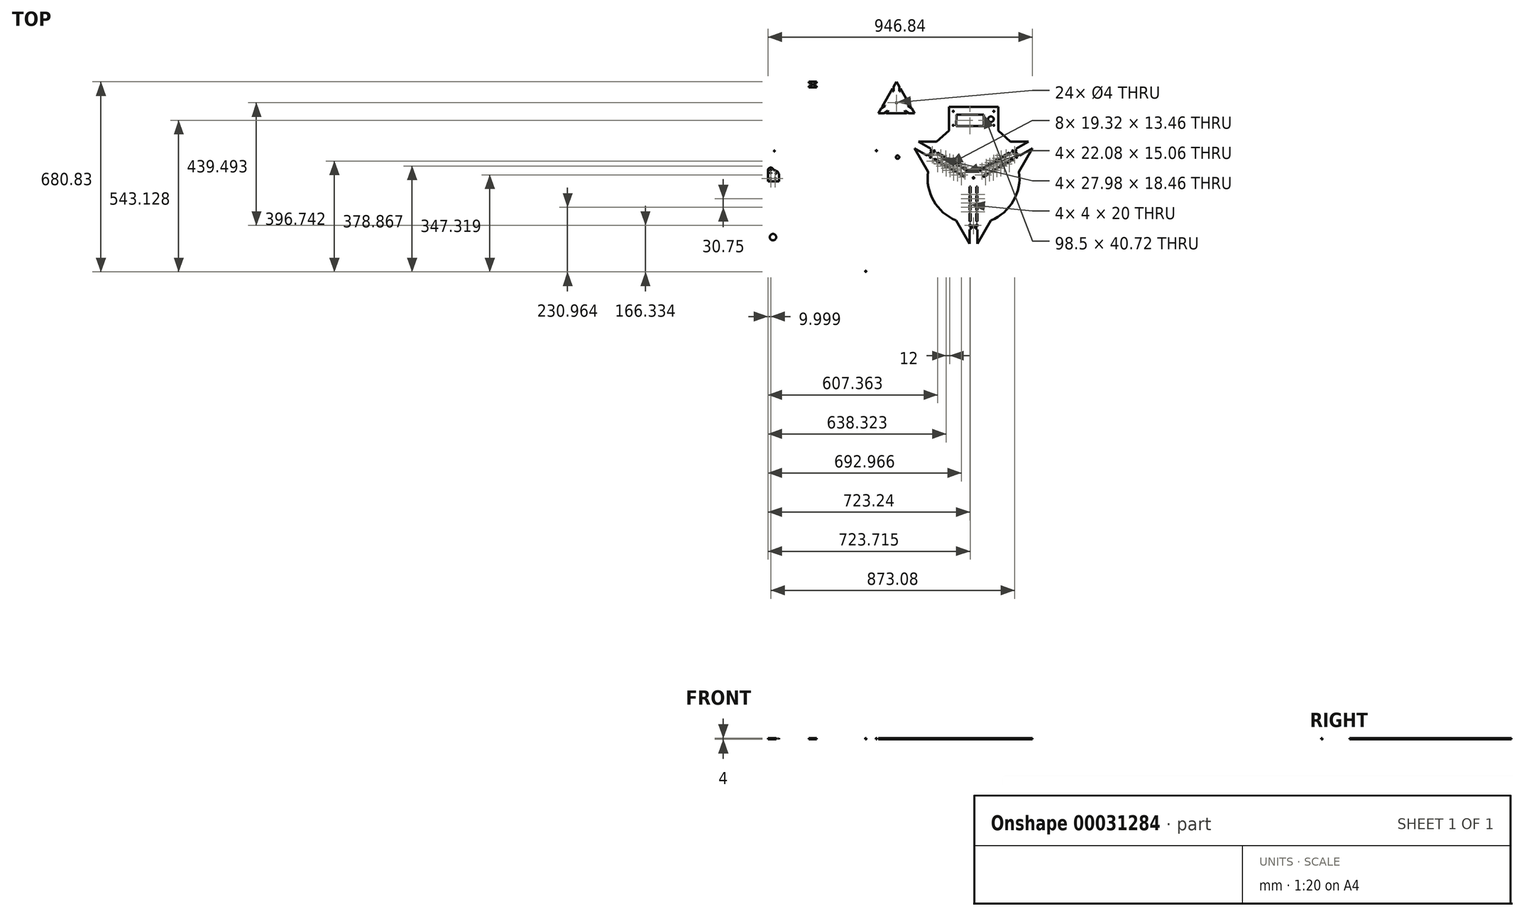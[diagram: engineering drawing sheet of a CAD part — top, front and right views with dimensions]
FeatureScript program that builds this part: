
annotation { "Feature Type Name" : "Feature", "Feature Type Description" : "" }
export const myFeature = defineFeature(function(context is Context, id is Id, definition is map)
    precondition{}
    {
        {
            var Q0;
            Q0=qCreatedBy(makeId("Top.planeOp"),FACE);
            var sketch = newSketch(context, id + "F0", { "sketchPlane" : qUnion([Q0])});
            skCircle(sketch, "E0", {"center": v(-448.83, 54.99) * mm, "radius": 1.5 * mm});
            skCircle(sketch, "E1", {"center": v(-448.8, 86.08) * mm, "radius": 1.5 * mm});
            skCircle(sketch, "E2", {"center": v(-453.84, -253.52) * mm, "radius": 11.5 * mm});
            skCircle(sketch, "E3", {"center": v(-386.12, -280.64) * mm, "radius": 2 * mm});
            skCircle(sketch, "E4", {"center": v(-423.42, -280.64) * mm, "radius": 2 * mm});
            skCircle(sketch, "E5", {"center": v(-469.5, -280.64) * mm, "radius": 2 * mm});
            skCircle(sketch, "E6", {"center": v(-438.44, -237.96) * mm, "radius": 1.5 * mm});
            skCircle(sketch, "E7", {"center": v(-469.53, -237.9) * mm, "radius": 1.5 * mm});
            skCircle(sketch, "E8", {"center": v(-439.73, -262.53) * mm, "radius": 1.5 * mm});
            skCircle(sketch, "E9", {"center": v(-448.28, -269) * mm, "radius": 1.5 * mm});
            skCircle(sketch, "E10", {"center": v(-438.44, -291.39) * mm, "radius": 1.5 * mm});
            skCircle(sketch, "E11", {"center": v(-469.55, -291.39) * mm, "radius": 1.5 * mm});
            skCircle(sketch, "E12", {"center": v(-469.55, -269) * mm, "radius": 1.5 * mm});
            skCircle(sketch, "E13", {"center": v(-83.7, 56.02) * mm, "radius": 2 * mm});
            skCircle(sketch, "E14", {"center": v(-231.13, -199.23) * mm, "radius": 2 * mm});
            skCircle(sketch, "E15", {"center": v(-378.53, 55.85) * mm, "radius": 2 * mm});
            skCircle(sketch, "E16", {"center": v(-231.13, -29.98) * mm, "radius": 177.5 * mm});
            skLineSegment(sketch, "E17", {"start": v(-11.84, 302.96) * mm, "end": v(-1.84, 285.64) * mm});
            skLineSegment(sketch, "E18", {"start": v(-1.84, 285.64) * mm, "end": v(-1.84, 258.8) * mm});
            skLineSegment(sketch, "E19", {"start": v(-1.84, 258.8) * mm, "end": v(2.16, 258.8) * mm});
            skLineSegment(sketch, "E20", {"start": v(2.16, 258.8) * mm, "end": v(2.16, 278.7) * mm});
            skLineSegment(sketch, "E21", {"start": v(2.16, 278.7) * mm, "end": v(39.1, 214.7) * mm});
            skLineSegment(sketch, "E22", {"start": v(39.1, 214.7) * mm, "end": v(21.87, 224.66) * mm});
            skLineSegment(sketch, "E23", {"start": v(21.87, 224.66) * mm, "end": v(19.87, 221.2) * mm});
            skLineSegment(sketch, "E24", {"start": v(19.87, 221.2) * mm, "end": v(43.1, 207.78) * mm});
            skLineSegment(sketch, "E25", {"start": v(43.1, 207.78) * mm, "end": v(53.1, 190.46) * mm});
            skLineSegment(sketch, "E26", {"start": v(53.1, 190.46) * mm, "end": v(33.1, 190.46) * mm});
            skLineSegment(sketch, "E27", {"start": v(33.1, 190.46) * mm, "end": v(9.87, 203.88) * mm});
            skLineSegment(sketch, "E28", {"start": v(9.87, 203.88) * mm, "end": v(7.87, 200.41) * mm});
            skLineSegment(sketch, "E29", {"start": v(7.87, 200.41) * mm, "end": v(25.1, 190.46) * mm});
            skLineSegment(sketch, "E30", {"start": v(25.1, 190.46) * mm, "end": v(-48.8, 190.46) * mm});
            skLineSegment(sketch, "E31", {"start": v(-48.8, 190.46) * mm, "end": v(-31.55, 200.41) * mm});
            skLineSegment(sketch, "E32", {"start": v(-31.55, 200.41) * mm, "end": v(-33.55, 203.88) * mm});
            skLineSegment(sketch, "E33", {"start": v(-33.55, 203.88) * mm, "end": v(-56.8, 190.46) * mm});
            skLineSegment(sketch, "E34", {"start": v(-56.8, 190.46) * mm, "end": v(-76.8, 190.46) * mm});
            skLineSegment(sketch, "E35", {"start": v(-76.8, 190.46) * mm, "end": v(-66.8, 207.78) * mm});
            skLineSegment(sketch, "E36", {"start": v(-66.8, 207.78) * mm, "end": v(-43.55, 221.2) * mm});
            skLineSegment(sketch, "E37", {"start": v(-43.55, 221.2) * mm, "end": v(-45.55, 224.66) * mm});
            skLineSegment(sketch, "E38", {"start": v(-45.55, 224.66) * mm, "end": v(-62.8, 214.7) * mm});
            skLineSegment(sketch, "E39", {"start": v(-62.8, 214.7) * mm, "end": v(-25.84, 278.7) * mm});
            skLineSegment(sketch, "E40", {"start": v(-25.84, 278.7) * mm, "end": v(-25.84, 258.8) * mm});
            skLineSegment(sketch, "E41", {"start": v(-25.84, 258.8) * mm, "end": v(-21.84, 258.8) * mm});
            skLineSegment(sketch, "E42", {"start": v(-21.84, 258.8) * mm, "end": v(-21.84, 285.64) * mm});
            skLineSegment(sketch, "E43", {"start": v(-21.84, 285.64) * mm, "end": v(-11.84, 302.96) * mm});
            skLineSegment(sketch, "E44", {"start": v(-314.86, 291.44) * mm, "end": v(-314.86, 289.44) * mm});
            skLineSegment(sketch, "E45", {"start": v(-314.86, 289.44) * mm, "end": v(-318.06, 289.45) * mm});
            skLineSegment(sketch, "E46", {"start": v(-318.06, 289.45) * mm, "end": v(-318.06, 291.45) * mm});
            skLineSegment(sketch, "E47", {"start": v(-318.06, 291.45) * mm, "end": v(-321.05, 291.44) * mm});
            skLineSegment(sketch, "E48", {"start": v(-321.05, 291.44) * mm, "end": v(-321.05, 287.57) * mm});
            skLineSegment(sketch, "E49", {"start": v(-325, 287.57) * mm, "end": v(-325, 282.96) * mm});
            skLineSegment(sketch, "E50", {"start": v(-314.88, 291.44) * mm, "end": v(-314.86, 291.44) * mm});
            skLineSegment(sketch, "E51", {"start": v(-314.86, 291.44) * mm, "end": v(-312.83, 291.44) * mm});
            skLineSegment(sketch, "E52", {"start": v(-312.83, 291.44) * mm, "end": v(-312.83, 294.44) * mm});
            skLineSegment(sketch, "E53", {"start": v(-312.83, 294.44) * mm, "end": v(-314.81, 294.44) * mm});
            skLineSegment(sketch, "E54", {"start": v(-314.81, 294.44) * mm, "end": v(-314.86, 294.44) * mm});
            skLineSegment(sketch, "E55", {"start": v(-314.86, 294.44) * mm, "end": v(-314.86, 296.44) * mm});
            skLineSegment(sketch, "E56", {"start": v(-314.86, 296.44) * mm, "end": v(-318.06, 296.45) * mm});
            skLineSegment(sketch, "E57", {"start": v(-318.06, 296.45) * mm, "end": v(-318.06, 294.44) * mm});
            skLineSegment(sketch, "E58", {"start": v(-318.06, 294.44) * mm, "end": v(-321.05, 294.44) * mm});
            skLineSegment(sketch, "E59", {"start": v(-321.05, 294.44) * mm, "end": v(-321.05, 298.32) * mm});
            skLineSegment(sketch, "E60", {"start": v(-321.05, 298.32) * mm, "end": v(-325, 298.32) * mm});
            skLineSegment(sketch, "E61", {"start": v(-325, 298.32) * mm, "end": v(-325, 302.96) * mm});
            skLineSegment(sketch, "E62", {"start": v(-461.5, -205.94) * mm, "end": v(-452.17, -195.94) * mm});
            skLineSegment(sketch, "E63", {"start": v(-452.17, -195.94) * mm, "end": v(-452, -195.94) * mm});
            skLineSegment(sketch, "E64", {"start": v(-452, -195.94) * mm, "end": v(-451.98, -195.73) * mm});
            skLineSegment(sketch, "E65", {"start": v(-451.98, -195.73) * mm, "end": v(-447.3, -190.7) * mm});
            skLineSegment(sketch, "E66", {"start": v(-447.3, -190.7) * mm, "end": v(-442.5, -195.94) * mm});
            skLineSegment(sketch, "E67", {"start": v(-442.5, -195.94) * mm, "end": v(-452, -205.94) * mm});
            skLineSegment(sketch, "E68", {"start": v(-452, -205.94) * mm, "end": v(-461.5, -205.94) * mm});
            skLineSegment(sketch, "E69", {"start": v(-442.5, -144.44) * mm, "end": v(-447.25, -149.62) * mm});
            skLineSegment(sketch, "E70", {"start": v(-447.25, -149.62) * mm, "end": v(-456.75, -149.62) * mm});
            skLineSegment(sketch, "E71", {"start": v(-456.75, -149.62) * mm, "end": v(-461.5, -144.44) * mm});
            skLineSegment(sketch, "E72", {"start": v(-461.5, -144.44) * mm, "end": v(-452, -144.44) * mm});
            skLineSegment(sketch, "E73", {"start": v(-452, -144.44) * mm, "end": v(-461.5, -134.44) * mm});
            skLineSegment(sketch, "E74", {"start": v(-461.5, -134.44) * mm, "end": v(-456.7, -129.2) * mm});
            skLineSegment(sketch, "E75", {"start": v(-456.7, -129.2) * mm, "end": v(-442.5, -144.44) * mm});
            skLineSegment(sketch, "E76", {"start": v(-442.5, -113.69) * mm, "end": v(-447.3, -118.92) * mm});
            skLineSegment(sketch, "E77", {"start": v(-447.3, -118.92) * mm, "end": v(-461.5, -103.69) * mm});
            skLineSegment(sketch, "E78", {"start": v(-461.5, -103.69) * mm, "end": v(-451.82, -103.69) * mm});
            skLineSegment(sketch, "E79", {"start": v(-451.82, -103.69) * mm, "end": v(-442.5, -113.69) * mm});
            skLineSegment(sketch, "E80", {"start": v(-461.5, -175.19) * mm, "end": v(-452, -165.19) * mm});
            skLineSegment(sketch, "E81", {"start": v(-452, -165.19) * mm, "end": v(-461.5, -165.19) * mm});
            skLineSegment(sketch, "E82", {"start": v(-461.5, -165.19) * mm, "end": v(-456.75, -160) * mm});
            skLineSegment(sketch, "E83", {"start": v(-456.75, -160) * mm, "end": v(-447.34, -160) * mm});
            skLineSegment(sketch, "E84", {"start": v(-447.34, -160) * mm, "end": v(-442.67, -165.19) * mm});
            skLineSegment(sketch, "E85", {"start": v(-442.67, -165.19) * mm, "end": v(-456.73, -180.4) * mm});
            skLineSegment(sketch, "E86", {"start": v(-456.73, -180.4) * mm, "end": v(-461.5, -175.19) * mm});
            skLineSegment(sketch, "E87", {"start": v(-465.48, -225.19) * mm, "end": v(-469.48, -225.19) * mm});
            skLineSegment(sketch, "E88", {"start": v(-465.48, -205.19) * mm, "end": v(-469.48, -205.19) * mm});
            skLineSegment(sketch, "E89", {"start": v(-469.48, -205.19) * mm, "end": v(-469.48, -209.84) * mm});
            skLineSegment(sketch, "E90", {"start": v(-469.48, -209.84) * mm, "end": v(-465.48, -209.84) * mm});
            skLineSegment(sketch, "E91", {"start": v(-465.48, -209.84) * mm, "end": v(-465.48, -205.19) * mm});
            skLineSegment(sketch, "E92", {"start": v(-465.48, -225.19) * mm, "end": v(-465.48, -220.59) * mm});
            skLineSegment(sketch, "E93", {"start": v(-465.48, -220.59) * mm, "end": v(-469.48, -220.59) * mm});
            skLineSegment(sketch, "E94", {"start": v(-469.48, -220.59) * mm, "end": v(-469.48, -225.19) * mm});
            skLineSegment(sketch, "E95", {"start": v(-465.57, -172.33) * mm, "end": v(-469.57, -172.33) * mm});
            skLineSegment(sketch, "E96", {"start": v(-465.57, -152.33) * mm, "end": v(-469.57, -152.33) * mm});
            skLineSegment(sketch, "E97", {"start": v(-469.57, -152.33) * mm, "end": v(-469.57, -156.98) * mm});
            skLineSegment(sketch, "E98", {"start": v(-469.57, -156.98) * mm, "end": v(-465.57, -156.98) * mm});
            skLineSegment(sketch, "E99", {"start": v(-465.57, -156.98) * mm, "end": v(-465.57, -152.33) * mm});
            skLineSegment(sketch, "E100", {"start": v(-465.57, -172.33) * mm, "end": v(-465.57, -167.73) * mm});
            skLineSegment(sketch, "E101", {"start": v(-465.57, -167.73) * mm, "end": v(-469.57, -167.73) * mm});
            skLineSegment(sketch, "E102", {"start": v(-469.57, -167.73) * mm, "end": v(-469.57, -172.33) * mm});
            skLineSegment(sketch, "E103", {"start": v(-439.62, -125.5) * mm, "end": v(-439.58, -125.5) * mm});
            skLineSegment(sketch, "E104", {"start": v(-439.58, -125.5) * mm, "end": v(-439.2, -125.56) * mm});
            skLineSegment(sketch, "E105", {"start": v(-439.2, -125.56) * mm, "end": v(-439.19, -127.56) * mm});
            skLineSegment(sketch, "E106", {"start": v(-439.19, -127.56) * mm, "end": v(-435.99, -127.56) * mm});
            skLineSegment(sketch, "E107", {"start": v(-435.99, -127.56) * mm, "end": v(-436, -125.56) * mm});
            skLineSegment(sketch, "E108", {"start": v(-436, -125.56) * mm, "end": v(-433, -125.56) * mm});
            skLineSegment(sketch, "E109", {"start": v(-433, -125.56) * mm, "end": v(-433, -129.44) * mm});
            skLineSegment(sketch, "E110", {"start": v(-433, -129.44) * mm, "end": v(-429, -129.44) * mm});
            skLineSegment(sketch, "E111", {"start": v(-429, -129.44) * mm, "end": v(-429, -149.44) * mm});
            skLineSegment(sketch, "E112", {"start": v(-429, -149.44) * mm, "end": v(-433, -149.44) * mm});
            skLineSegment(sketch, "E113", {"start": v(-433, -149.44) * mm, "end": v(-433, -153.31) * mm});
            skLineSegment(sketch, "E114", {"start": v(-433, -153.31) * mm, "end": v(-435.97, -153.31) * mm});
            skLineSegment(sketch, "E115", {"start": v(-435.97, -153.31) * mm, "end": v(-435.97, -151.31) * mm});
            skLineSegment(sketch, "E116", {"start": v(-435.97, -151.31) * mm, "end": v(-439.17, -151.31) * mm});
            skLineSegment(sketch, "E117", {"start": v(-439.17, -151.31) * mm, "end": v(-439.17, -153.3) * mm});
            skLineSegment(sketch, "E118", {"start": v(-439.24, -156.3) * mm, "end": v(-439.17, -156.3) * mm});
            skLineSegment(sketch, "E119", {"start": v(-439.17, -156.3) * mm, "end": v(-439.16, -158.31) * mm});
            skLineSegment(sketch, "E120", {"start": v(-439.16, -158.31) * mm, "end": v(-435.96, -158.31) * mm});
            skLineSegment(sketch, "E121", {"start": v(-435.96, -158.31) * mm, "end": v(-435.97, -156.3) * mm});
            skLineSegment(sketch, "E122", {"start": v(-435.97, -156.3) * mm, "end": v(-433, -156.31) * mm});
            skLineSegment(sketch, "E123", {"start": v(-433, -156.31) * mm, "end": v(-433, -160.19) * mm});
            skLineSegment(sketch, "E124", {"start": v(-433, -160.19) * mm, "end": v(-429, -160.19) * mm});
            skLineSegment(sketch, "E125", {"start": v(-429, -160.19) * mm, "end": v(-429, -180.19) * mm});
            skLineSegment(sketch, "E126", {"start": v(-429, -180.19) * mm, "end": v(-433, -180.19) * mm});
            skLineSegment(sketch, "E127", {"start": v(-433, -180.19) * mm, "end": v(-433, -184.06) * mm});
            skLineSegment(sketch, "E128", {"start": v(-433, -184.06) * mm, "end": v(-435.94, -184.06) * mm});
            skLineSegment(sketch, "E129", {"start": v(-435.94, -184.06) * mm, "end": v(-435.94, -182.06) * mm});
            skLineSegment(sketch, "E130", {"start": v(-435.94, -182.06) * mm, "end": v(-439.14, -182.06) * mm});
            skLineSegment(sketch, "E131", {"start": v(-439.14, -182.06) * mm, "end": v(-439.14, -184.06) * mm});
            skLineSegment(sketch, "E132", {"start": v(-439.14, -184.06) * mm, "end": v(-439.18, -184.07) * mm});
            skLineSegment(sketch, "E133", {"start": v(-439.14, -187.07) * mm, "end": v(-439.14, -189.06) * mm});
            skLineSegment(sketch, "E134", {"start": v(-439.14, -189.06) * mm, "end": v(-435.94, -189.06) * mm});
            skLineSegment(sketch, "E135", {"start": v(-435.94, -189.06) * mm, "end": v(-435.94, -187.06) * mm});
            skLineSegment(sketch, "E136", {"start": v(-435.94, -187.06) * mm, "end": v(-433, -187.06) * mm});
            skLineSegment(sketch, "E137", {"start": v(-433, -187.06) * mm, "end": v(-433, -190.94) * mm});
            skLineSegment(sketch, "E138", {"start": v(-433, -190.94) * mm, "end": v(-429, -190.94) * mm});
            skLineSegment(sketch, "E139", {"start": v(-429, -190.94) * mm, "end": v(-429, -220.94) * mm});
            skLineSegment(sketch, "E140", {"start": v(-429, -220.94) * mm, "end": v(-433, -220.94) * mm});
            skLineSegment(sketch, "E141", {"start": v(-433, -220.94) * mm, "end": v(-433, -230.82) * mm});
            skLineSegment(sketch, "E142", {"start": v(-433, -230.82) * mm, "end": v(-429, -230.82) * mm});
            skLineSegment(sketch, "E143", {"start": v(-429, -230.82) * mm, "end": v(-429, -238.82) * mm});
            skLineSegment(sketch, "E144", {"start": v(-429, -238.82) * mm, "end": v(-433, -238.82) * mm});
            skLineSegment(sketch, "E145", {"start": v(-433, -238.82) * mm, "end": v(-433, -249.24) * mm});
            skLineSegment(sketch, "E146", {"start": v(-433, -249.24) * mm, "end": v(-429, -249.24) * mm});
            skLineSegment(sketch, "E147", {"start": v(-429, -249.24) * mm, "end": v(-429, -257.24) * mm});
            skLineSegment(sketch, "E148", {"start": v(-429, -257.24) * mm, "end": v(-373, -270.43) * mm});
            skLineSegment(sketch, "E149", {"start": v(-373, -270.43) * mm, "end": v(-373, -290.43) * mm});
            skLineSegment(sketch, "E150", {"start": v(-373, -290.43) * mm, "end": v(-433, -302.96) * mm});
            skLineSegment(sketch, "E151", {"start": v(-433, -302.96) * mm, "end": v(-475, -302.96) * mm});
            skLineSegment(sketch, "E152", {"start": v(-475, -302.96) * mm, "end": v(-475, -95.5) * mm});
            skLineSegment(sketch, "E153", {"start": v(-475, -95.5) * mm, "end": v(-468.83, -95.5) * mm});
            skLineSegment(sketch, "E154", {"start": v(-468.83, -95.5) * mm, "end": v(-468.83, -106.93) * mm});
            skLineSegment(sketch, "E155", {"start": v(-468.83, -106.93) * mm, "end": v(-464.83, -106.93) * mm});
            skLineSegment(sketch, "E156", {"start": v(-464.83, -106.93) * mm, "end": v(-464.83, -95.5) * mm});
            skLineSegment(sketch, "E157", {"start": v(-464.83, -95.5) * mm, "end": v(-429, -95.5) * mm});
            skLineSegment(sketch, "E158", {"start": v(-429, -95.5) * mm, "end": v(-429, -118.69) * mm});
            skLineSegment(sketch, "E159", {"start": v(-429, -118.69) * mm, "end": v(-433, -118.69) * mm});
            skLineSegment(sketch, "E160", {"start": v(-433, -118.69) * mm, "end": v(-433, -122.56) * mm});
            skLineSegment(sketch, "E161", {"start": v(-433, -122.56) * mm, "end": v(-436, -122.56) * mm});
            skLineSegment(sketch, "E162", {"start": v(-436, -122.56) * mm, "end": v(-436, -120.56) * mm});
            skLineSegment(sketch, "E163", {"start": v(-436, -120.56) * mm, "end": v(-439.2, -120.56) * mm});
            skLineSegment(sketch, "E164", {"start": v(-439.2, -120.56) * mm, "end": v(-439.2, -122.56) * mm});
            skLineSegment(sketch, "E165", {"start": v(-439.2, -122.56) * mm, "end": v(-439.2, -122.56) * mm});
            skLineSegment(sketch, "E166", {"start": v(-439.18, -184.07) * mm, "end": v(-440.73, -184.07) * mm});
            skLineSegment(sketch, "E167", {"start": v(-440.73, -184.07) * mm, "end": v(-440.73, -187.07) * mm});
            skLineSegment(sketch, "E168", {"start": v(-440.73, -187.07) * mm, "end": v(-439.14, -187.07) * mm});
            skLineSegment(sketch, "E169", {"start": v(-439.2, -122.56) * mm, "end": v(-439.2, -122.5) * mm});
            skLineSegment(sketch, "E170", {"start": v(-439.2, -122.5) * mm, "end": v(-440.8, -122.5) * mm});
            skLineSegment(sketch, "E171", {"start": v(-440.8, -122.5) * mm, "end": v(-440.8, -125.5) * mm});
            skLineSegment(sketch, "E172", {"start": v(-440.8, -125.5) * mm, "end": v(-439.62, -125.5) * mm});
            skLineSegment(sketch, "E173", {"start": v(-439.17, -153.3) * mm, "end": v(-440.77, -153.3) * mm});
            skLineSegment(sketch, "E174", {"start": v(-440.77, -153.3) * mm, "end": v(-440.77, -156.3) * mm});
            skLineSegment(sketch, "E175", {"start": v(-440.77, -156.3) * mm, "end": v(-439.24, -156.3) * mm});
            skCircle(sketch, "E176", {"center": v(-452, -185.57) * mm, "radius": 4.5 * mm});
            skCircle(sketch, "E177", {"center": v(-452, -124) * mm, "radius": 4.5 * mm});
            skCircle(sketch, "E178", {"center": v(-467.5, -214.97) * mm, "radius": 1.5 * mm});
            skEllipse(sketch, "E179", {"center": v(-452.09, -222.76) * mm, "majorRadius": 9.41 * mm, "minorRadius": 1.97 * mm, "majorAxis": v(1, 0)});
            skCircle(sketch, "E180", {"center": v(-467.57, -162.23) * mm, "radius": 1.5 * mm});
            skEllipse(sketch, "E181", {"center": v(-455, -297.5) * mm, "majorRadius": 9.41 * mm, "minorRadius": 1.97 * mm, "majorAxis": v(1, 0)});
            skLineSegment(sketch, "E182", {"start": v(-451.93, 91.53) * mm, "end": v(-442.71, 91.53) * mm});
            skLineSegment(sketch, "E183", {"start": v(-442.75, 91.53) * mm, "end": v(-448.2, 71.57) * mm});
            skLineSegment(sketch, "E184", {"start": v(-448.2, 71.57) * mm, "end": v(-442.75, 49.53) * mm});
            skLineSegment(sketch, "E185", {"start": v(-442.71, 49.53) * mm, "end": v(-451.93, 49.53) * mm});
            skLineSegment(sketch, "E186", {"start": v(-451.84, 49.53) * mm, "end": v(-457.28, 71.57) * mm});
            skLineSegment(sketch, "E187", {"start": v(-457.28, 71.57) * mm, "end": v(-451.84, 91.53) * mm});
            skLineSegment(sketch, "E188", {"start": v(-431.84, -33.47) * mm, "end": v(-431.84, -53.47) * mm});
            skLineSegment(sketch, "E189", {"start": v(-471.84, -53.47) * mm, "end": v(-471.84, -13.47) * mm});
            skLineSegment(sketch, "E190", {"start": v(-471.84, -13.47) * mm, "end": v(-471.83, -13.37) * mm});
            skLineSegment(sketch, "E191", {"start": v(421.7, 33.58) * mm, "end": v(419.7, 37.04) * mm});
            skLineSegment(sketch, "E192", {"start": v(419.7, 37.04) * mm, "end": v(412.77, 33.04) * mm});
            skLineSegment(sketch, "E193", {"start": v(412.77, 33.04) * mm, "end": v(414.77, 29.58) * mm});
            skLineSegment(sketch, "E194", {"start": v(414.77, 29.58) * mm, "end": v(421.7, 33.58) * mm});
            skLineSegment(sketch, "E195", {"start": v(277.88, -207.54) * mm, "end": v(273.88, -207.54) * mm});
            skLineSegment(sketch, "E196", {"start": v(273.88, -207.54) * mm, "end": v(273.88, -215.54) * mm});
            skLineSegment(sketch, "E197", {"start": v(273.88, -215.54) * mm, "end": v(277.88, -215.54) * mm});
            skLineSegment(sketch, "E198", {"start": v(277.88, -215.54) * mm, "end": v(277.88, -207.54) * mm});
            skLineSegment(sketch, "E199", {"start": v(120.05, 57.83) * mm, "end": v(118.05, 54.36) * mm});
            skLineSegment(sketch, "E200", {"start": v(118.05, 54.36) * mm, "end": v(124.98, 50.36) * mm});
            skLineSegment(sketch, "E201", {"start": v(124.98, 50.36) * mm, "end": v(126.98, 53.83) * mm});
            skLineSegment(sketch, "E202", {"start": v(126.98, 53.83) * mm, "end": v(120.05, 57.83) * mm});
            skLineSegment(sketch, "E203", {"start": v(214.77, 3.14) * mm, "end": v(197.45, 13.14) * mm});
            skLineSegment(sketch, "E204", {"start": v(197.45, 13.14) * mm, "end": v(195.45, 9.67) * mm});
            skLineSegment(sketch, "E205", {"start": v(195.45, 9.67) * mm, "end": v(212.77, -0.33) * mm});
            skLineSegment(sketch, "E206", {"start": v(212.77, -0.33) * mm, "end": v(214.77, 3.14) * mm});
            skLineSegment(sketch, "E207", {"start": v(224.08, -2.24) * mm, "end": v(222.08, -5.7) * mm});
            skLineSegment(sketch, "E208", {"start": v(222.08, -5.7) * mm, "end": v(242.17, -17.3) * mm});
            skLineSegment(sketch, "E209", {"start": v(242.17, -17.3) * mm, "end": v(244.17, -13.83) * mm});
            skLineSegment(sketch, "E210", {"start": v(244.17, -13.83) * mm, "end": v(224.08, -2.24) * mm});
            skLineSegment(sketch, "E211", {"start": v(212.08, -23.02) * mm, "end": v(210.08, -26.49) * mm});
            skLineSegment(sketch, "E212", {"start": v(210.08, -26.49) * mm, "end": v(230.17, -38.08) * mm});
            skLineSegment(sketch, "E213", {"start": v(230.17, -38.08) * mm, "end": v(232.17, -34.62) * mm});
            skLineSegment(sketch, "E214", {"start": v(232.17, -34.62) * mm, "end": v(212.08, -23.02) * mm});
            skLineSegment(sketch, "E215", {"start": v(185.45, -7.65) * mm, "end": v(183.45, -11.11) * mm});
            skLineSegment(sketch, "E216", {"start": v(183.45, -11.11) * mm, "end": v(200.77, -21.11) * mm});
            skLineSegment(sketch, "E217", {"start": v(200.77, -21.11) * mm, "end": v(202.77, -17.65) * mm});
            skLineSegment(sketch, "E218", {"start": v(202.77, -17.65) * mm, "end": v(185.45, -7.65) * mm});
            skLineSegment(sketch, "E219", {"start": v(174.14, -5.74) * mm, "end": v(176.14, -2.27) * mm});
            skLineSegment(sketch, "E220", {"start": v(176.14, -2.27) * mm, "end": v(158.82, 7.73) * mm});
            skLineSegment(sketch, "E221", {"start": v(158.82, 7.73) * mm, "end": v(156.82, 4.26) * mm});
            skLineSegment(sketch, "E222", {"start": v(156.82, 4.26) * mm, "end": v(174.14, -5.74) * mm});
            skLineSegment(sketch, "E223", {"start": v(188.14, 18.51) * mm, "end": v(170.82, 28.51) * mm});
            skLineSegment(sketch, "E224", {"start": v(170.82, 28.51) * mm, "end": v(168.82, 25.05) * mm});
            skLineSegment(sketch, "E225", {"start": v(168.82, 25.05) * mm, "end": v(186.14, 15.05) * mm});
            skLineSegment(sketch, "E226", {"start": v(186.14, 15.05) * mm, "end": v(188.14, 18.51) * mm});
            skLineSegment(sketch, "E227", {"start": v(161.51, 33.89) * mm, "end": v(135.53, 48.89) * mm});
            skLineSegment(sketch, "E228", {"start": v(135.53, 48.89) * mm, "end": v(133.53, 45.42) * mm});
            skLineSegment(sketch, "E229", {"start": v(133.53, 45.42) * mm, "end": v(159.51, 30.42) * mm});
            skLineSegment(sketch, "E230", {"start": v(159.51, 30.42) * mm, "end": v(161.51, 33.89) * mm});
            skLineSegment(sketch, "E231", {"start": v(149.51, 13.1) * mm, "end": v(123.53, 28.1) * mm});
            skLineSegment(sketch, "E232", {"start": v(123.53, 28.1) * mm, "end": v(121.53, 24.64) * mm});
            skLineSegment(sketch, "E233", {"start": v(121.53, 24.64) * mm, "end": v(147.51, 9.64) * mm});
            skLineSegment(sketch, "E234", {"start": v(147.51, 9.64) * mm, "end": v(149.51, 13.1) * mm});
            skLineSegment(sketch, "E235", {"start": v(249.88, -95.4) * mm, "end": v(253.88, -95.4) * mm});
            skLineSegment(sketch, "E236", {"start": v(253.88, -95.4) * mm, "end": v(253.88, -72.21) * mm});
            skLineSegment(sketch, "E237", {"start": v(253.88, -72.21) * mm, "end": v(249.88, -72.21) * mm});
            skLineSegment(sketch, "E238", {"start": v(249.88, -72.21) * mm, "end": v(249.88, -95.4) * mm});
            skLineSegment(sketch, "E239", {"start": v(273.88, -95.4) * mm, "end": v(277.88, -95.4) * mm});
            skLineSegment(sketch, "E240", {"start": v(277.88, -95.4) * mm, "end": v(277.88, -72.21) * mm});
            skLineSegment(sketch, "E241", {"start": v(277.88, -72.21) * mm, "end": v(273.88, -72.21) * mm});
            skLineSegment(sketch, "E242", {"start": v(273.88, -72.21) * mm, "end": v(273.88, -95.4) * mm});
            skLineSegment(sketch, "E243", {"start": v(273.88, -126.16) * mm, "end": v(277.88, -126.16) * mm});
            skLineSegment(sketch, "E244", {"start": v(277.88, -126.16) * mm, "end": v(277.88, -106.16) * mm});
            skLineSegment(sketch, "E245", {"start": v(277.88, -106.16) * mm, "end": v(273.88, -106.16) * mm});
            skLineSegment(sketch, "E246", {"start": v(273.88, -106.16) * mm, "end": v(273.88, -126.16) * mm});
            skLineSegment(sketch, "E247", {"start": v(249.88, -126.16) * mm, "end": v(253.88, -126.16) * mm});
            skLineSegment(sketch, "E248", {"start": v(253.88, -126.16) * mm, "end": v(253.88, -106.16) * mm});
            skLineSegment(sketch, "E249", {"start": v(253.88, -106.16) * mm, "end": v(249.88, -106.16) * mm});
            skLineSegment(sketch, "E250", {"start": v(249.88, -106.16) * mm, "end": v(249.88, -126.16) * mm});
            skLineSegment(sketch, "E251", {"start": v(253.88, -136.9) * mm, "end": v(249.88, -136.9) * mm});
            skLineSegment(sketch, "E252", {"start": v(249.88, -136.9) * mm, "end": v(249.88, -156.9) * mm});
            skLineSegment(sketch, "E253", {"start": v(249.88, -156.9) * mm, "end": v(253.88, -156.9) * mm});
            skLineSegment(sketch, "E254", {"start": v(253.88, -156.9) * mm, "end": v(253.88, -136.9) * mm});
            skLineSegment(sketch, "E255", {"start": v(277.88, -136.9) * mm, "end": v(273.88, -136.9) * mm});
            skLineSegment(sketch, "E256", {"start": v(273.88, -136.9) * mm, "end": v(273.88, -156.9) * mm});
            skLineSegment(sketch, "E257", {"start": v(273.88, -156.9) * mm, "end": v(277.88, -156.9) * mm});
            skLineSegment(sketch, "E258", {"start": v(277.88, -156.9) * mm, "end": v(277.88, -136.9) * mm});
            skLineSegment(sketch, "E259", {"start": v(277.88, -167.66) * mm, "end": v(273.88, -167.66) * mm});
            skLineSegment(sketch, "E260", {"start": v(273.88, -167.66) * mm, "end": v(273.88, -197.66) * mm});
            skLineSegment(sketch, "E261", {"start": v(273.88, -197.66) * mm, "end": v(277.88, -197.66) * mm});
            skLineSegment(sketch, "E262", {"start": v(277.88, -197.66) * mm, "end": v(277.88, -167.66) * mm});
            skLineSegment(sketch, "E263", {"start": v(253.88, -167.66) * mm, "end": v(249.88, -167.66) * mm});
            skLineSegment(sketch, "E264", {"start": v(249.88, -167.66) * mm, "end": v(249.88, -197.66) * mm});
            skLineSegment(sketch, "E265", {"start": v(249.88, -197.66) * mm, "end": v(253.88, -197.66) * mm});
            skLineSegment(sketch, "E266", {"start": v(253.88, -197.66) * mm, "end": v(253.88, -167.66) * mm});
            skLineSegment(sketch, "E267", {"start": v(351.6, -2.27) * mm, "end": v(353.6, -5.74) * mm});
            skLineSegment(sketch, "E268", {"start": v(353.6, -5.74) * mm, "end": v(370.93, 4.26) * mm});
            skLineSegment(sketch, "E269", {"start": v(370.93, 4.26) * mm, "end": v(368.93, 7.73) * mm});
            skLineSegment(sketch, "E270", {"start": v(368.93, 7.73) * mm, "end": v(351.6, -2.27) * mm});
            skLineSegment(sketch, "E271", {"start": v(366.24, 33.89) * mm, "end": v(368.24, 30.42) * mm});
            skLineSegment(sketch, "E272", {"start": v(368.24, 30.42) * mm, "end": v(394.22, 45.42) * mm});
            skLineSegment(sketch, "E273", {"start": v(394.22, 45.42) * mm, "end": v(392.22, 48.89) * mm});
            skLineSegment(sketch, "E274", {"start": v(392.22, 48.89) * mm, "end": v(366.24, 33.89) * mm});
            skLineSegment(sketch, "E275", {"start": v(339.6, 18.51) * mm, "end": v(341.6, 15.05) * mm});
            skLineSegment(sketch, "E276", {"start": v(341.6, 15.05) * mm, "end": v(358.93, 25.05) * mm});
            skLineSegment(sketch, "E277", {"start": v(358.93, 25.05) * mm, "end": v(356.93, 28.51) * mm});
            skLineSegment(sketch, "E278", {"start": v(356.93, 28.51) * mm, "end": v(339.6, 18.51) * mm});
            skLineSegment(sketch, "E279", {"start": v(312.98, 3.14) * mm, "end": v(314.98, -0.33) * mm});
            skLineSegment(sketch, "E280", {"start": v(314.98, -0.33) * mm, "end": v(332.3, 9.67) * mm});
            skLineSegment(sketch, "E281", {"start": v(332.3, 9.67) * mm, "end": v(330.3, 13.14) * mm});
            skLineSegment(sketch, "E282", {"start": v(330.3, 13.14) * mm, "end": v(312.98, 3.14) * mm});
            skLineSegment(sketch, "E283", {"start": v(324.98, -17.65) * mm, "end": v(326.98, -21.11) * mm});
            skLineSegment(sketch, "E284", {"start": v(326.98, -21.11) * mm, "end": v(344.3, -11.11) * mm});
            skLineSegment(sketch, "E285", {"start": v(344.3, -11.11) * mm, "end": v(342.3, -7.65) * mm});
            skLineSegment(sketch, "E286", {"start": v(342.3, -7.65) * mm, "end": v(324.98, -17.65) * mm});
            skLineSegment(sketch, "E287", {"start": v(303.67, -2.24) * mm, "end": v(283.58, -13.83) * mm});
            skLineSegment(sketch, "E288", {"start": v(283.58, -13.83) * mm, "end": v(285.58, -17.3) * mm});
            skLineSegment(sketch, "E289", {"start": v(285.58, -17.3) * mm, "end": v(305.67, -5.7) * mm});
            skLineSegment(sketch, "E290", {"start": v(305.67, -5.7) * mm, "end": v(303.67, -2.24) * mm});
            skLineSegment(sketch, "E291", {"start": v(315.67, -23.02) * mm, "end": v(295.58, -34.62) * mm});
            skLineSegment(sketch, "E292", {"start": v(295.58, -34.62) * mm, "end": v(297.58, -38.08) * mm});
            skLineSegment(sketch, "E293", {"start": v(297.58, -38.08) * mm, "end": v(317.67, -26.49) * mm});
            skLineSegment(sketch, "E294", {"start": v(317.67, -26.49) * mm, "end": v(315.67, -23.02) * mm});
            skLineSegment(sketch, "E295", {"start": v(400.77, 53.83) * mm, "end": v(402.77, 50.36) * mm});
            skLineSegment(sketch, "E296", {"start": v(402.77, 50.36) * mm, "end": v(409.7, 54.36) * mm});
            skLineSegment(sketch, "E297", {"start": v(409.7, 54.36) * mm, "end": v(407.7, 57.83) * mm});
            skLineSegment(sketch, "E298", {"start": v(407.7, 57.83) * mm, "end": v(400.77, 53.83) * mm});
            skLineSegment(sketch, "E299", {"start": v(404.22, 28.1) * mm, "end": v(378.24, 13.1) * mm});
            skLineSegment(sketch, "E300", {"start": v(378.24, 13.1) * mm, "end": v(380.24, 9.64) * mm});
            skLineSegment(sketch, "E301", {"start": v(380.24, 9.64) * mm, "end": v(406.22, 24.64) * mm});
            skLineSegment(sketch, "E302", {"start": v(406.22, 24.64) * mm, "end": v(404.22, 28.1) * mm});
            skLineSegment(sketch, "E303", {"start": v(112.98, 29.58) * mm, "end": v(114.98, 33.04) * mm});
            skLineSegment(sketch, "E304", {"start": v(114.98, 33.04) * mm, "end": v(108.05, 37.04) * mm});
            skLineSegment(sketch, "E305", {"start": v(108.05, 37.04) * mm, "end": v(106.05, 33.58) * mm});
            skLineSegment(sketch, "E306", {"start": v(106.05, 33.58) * mm, "end": v(112.98, 29.58) * mm});
            skLineSegment(sketch, "E307", {"start": v(66.75, 88.6) * mm, "end": v(131.72, 88.6) * mm});
            skLineSegment(sketch, "E308", {"start": v(461, 88.6) * mm, "end": v(416.73, 63.04) * mm});
            skLineSegment(sketch, "E309", {"start": v(416.73, 63.04) * mm, "end": v(418.73, 59.58) * mm});
            skLineSegment(sketch, "E310", {"start": v(412.63, 56.05) * mm, "end": v(422.62, 38.73) * mm});
            skLineSegment(sketch, "E311", {"start": v(428.73, 42.26) * mm, "end": v(430.73, 38.8) * mm});
            skLineSegment(sketch, "E312", {"start": v(430.73, 38.8) * mm, "end": v(475, 64.35) * mm});
            skLineSegment(sketch, "E313", {"start": v(475, 64.35) * mm, "end": v(426.76, -19.2) * mm});
            skLineSegment(sketch, "E314", {"start": v(326.1, -193.53) * mm, "end": v(277.88, -277.08) * mm});
            skLineSegment(sketch, "E315", {"start": v(277.88, -277.08) * mm, "end": v(277.88, -225.96) * mm});
            skLineSegment(sketch, "E316", {"start": v(277.88, -225.96) * mm, "end": v(273.88, -225.96) * mm});
            skLineSegment(sketch, "E317", {"start": v(273.88, -218.91) * mm, "end": v(253.88, -218.91) * mm});
            skLineSegment(sketch, "E318", {"start": v(253.88, -225.96) * mm, "end": v(249.88, -225.96) * mm});
            skLineSegment(sketch, "E319", {"start": v(249.88, -225.96) * mm, "end": v(249.88, -277.08) * mm});
            skLineSegment(sketch, "E320", {"start": v(249.88, -277.08) * mm, "end": v(201.64, -193.53) * mm});
            skLineSegment(sketch, "E321", {"start": v(100.99, -19.2) * mm, "end": v(52.75, 64.35) * mm});
            skLineSegment(sketch, "E322", {"start": v(52.75, 64.35) * mm, "end": v(97.02, 38.8) * mm});
            skLineSegment(sketch, "E323", {"start": v(97.02, 38.8) * mm, "end": v(99.02, 42.26) * mm});
            skLineSegment(sketch, "E324", {"start": v(105.13, 38.73) * mm, "end": v(115.13, 56.05) * mm});
            skLineSegment(sketch, "E325", {"start": v(109.02, 59.58) * mm, "end": v(111.02, 63.04) * mm});
            skLineSegment(sketch, "E326", {"start": v(111.02, 63.04) * mm, "end": v(66.75, 88.6) * mm});
            skLineSegment(sketch, "E327", {"start": v(253.88, -207.54) * mm, "end": v(249.88, -207.54) * mm});
            skLineSegment(sketch, "E328", {"start": v(249.88, -207.54) * mm, "end": v(249.88, -215.54) * mm});
            skLineSegment(sketch, "E329", {"start": v(249.88, -215.54) * mm, "end": v(253.88, -215.54) * mm});
            skLineSegment(sketch, "E330", {"start": v(253.88, -215.54) * mm, "end": v(253.88, -207.54) * mm});
            skLineSegment(sketch, "E331", {"start": v(99.02, 42.26) * mm, "end": v(105.13, 38.73) * mm});
            skLineSegment(sketch, "E332", {"start": v(109.02, 59.58) * mm, "end": v(115.13, 56.05) * mm});
            skCircle(sketch, "E333", {"center": v(116.51, 43.7) * mm, "radius": 2 * mm});
            skArc(sketch, "E334", {"start": v(100.99, -19.2) * mm, "mid": v(121.34, -123.67) * mm, "end": v(201.64, -193.53) * mm});
            skArc(sketch, "E335", {"start": v(326.1, -193.53) * mm, "mid": v(406.41, -123.67) * mm, "end": v(426.76, -19.2) * mm});
            skLineSegment(sketch, "E336", {"start": v(253.88, -225.96) * mm, "end": v(253.88, -218.91) * mm});
            skLineSegment(sketch, "E337", {"start": v(273.88, -218.91) * mm, "end": v(273.88, -225.96) * mm});
            skCircle(sketch, "E338", {"center": v(263.88, -211.54) * mm, "radius": 2 * mm});
            skLineSegment(sketch, "E339", {"start": v(428.73, 42.26) * mm, "end": v(422.62, 38.73) * mm});
            skLineSegment(sketch, "E340", {"start": v(412.63, 56.05) * mm, "end": v(418.73, 59.58) * mm});
            skCircle(sketch, "E341", {"center": v(411.24, 43.7) * mm, "radius": 2 * mm});
            skCircle(sketch, "E342", {"center": v(263.88, -41.38) * mm, "radius": 2.5 * mm});
            skLineSegment(sketch, "E343", {"start": v(263.88, -41.38) * mm, "end": v(263.88, 185.62) * mm, "construction": true});
            skLineSegment(sketch, "E344", {"start": v(251.88, -167.66) * mm, "end": v(251.88, -156.9) * mm, "construction": true});
            skLineSegment(sketch, "E345", {"start": v(275.88, -167.66) * mm, "end": v(275.88, -156.9) * mm, "construction": true});
            skLineSegment(sketch, "E346.trimOffspring", {"start": v(275.88, -136.9) * mm, "end": v(275.88, -126.16) * mm, "construction": true});
            skLineSegment(sketch, "E347.trimOffspring", {"start": v(251.88, -136.9) * mm, "end": v(251.88, -126.16) * mm, "construction": true});
            skLineSegment(sketch, "E348.trimOffspring", {"start": v(275.88, -106.16) * mm, "end": v(275.88, -95.4) * mm, "construction": true});
            skLineSegment(sketch, "E349.trimOffspring", {"start": v(251.88, -106.16) * mm, "end": v(251.88, -95.4) * mm, "construction": true});
            skCircle(sketch, "E350", {"center": v(251.88, -162.28) * mm, "radius": 2 * mm});
            skCircle(sketch, "E351", {"center": v(275.88, -162.28) * mm, "radius": 2 * mm});
            skCircle(sketch, "E352", {"center": v(251.88, -131.53) * mm, "radius": 2 * mm});
            skCircle(sketch, "E353", {"center": v(275.88, -131.53) * mm, "radius": 2 * mm});
            skCircle(sketch, "E354", {"center": v(251.88, -100.78) * mm, "radius": 2 * mm});
            skCircle(sketch, "E355", {"center": v(275.88, -100.78) * mm, "radius": 2 * mm});
            skLineSegment(sketch, "E356", {"start": v(316.67, -24.75) * mm, "end": v(325.98, -19.38) * mm, "construction": true});
            skLineSegment(sketch, "E357", {"start": v(304.67, -3.97) * mm, "end": v(313.98, 1.4) * mm, "construction": true});
            skLineSegment(sketch, "E358.trimOffspring", {"start": v(331.3, 11.4) * mm, "end": v(340.6, 16.78) * mm, "construction": true});
            skLineSegment(sketch, "E359.trimOffspring", {"start": v(343.3, -9.38) * mm, "end": v(352.6, -4) * mm, "construction": true});
            skLineSegment(sketch, "E360.trimOffspring", {"start": v(369.93, 6) * mm, "end": v(379.24, 11.37) * mm, "construction": true});
            skLineSegment(sketch, "E361.trimOffspring", {"start": v(357.93, 26.78) * mm, "end": v(367.24, 32.16) * mm, "construction": true});
            skCircle(sketch, "E362", {"center": v(321.32, -22.07) * mm, "radius": 2 * mm});
            skCircle(sketch, "E363", {"center": v(309.32, -1.28) * mm, "radius": 2 * mm});
            skCircle(sketch, "E364", {"center": v(347.95, -6.7) * mm, "radius": 2 * mm});
            skCircle(sketch, "E365", {"center": v(335.95, 14.1) * mm, "radius": 2 * mm});
            skCircle(sketch, "E366", {"center": v(374.58, 8.68) * mm, "radius": 2 * mm});
            skCircle(sketch, "E367", {"center": v(362.58, 29.47) * mm, "radius": 2 * mm});
            skLineSegment(sketch, "E368", {"start": v(211.08, -24.75) * mm, "end": v(201.77, -19.38) * mm, "construction": true});
            skLineSegment(sketch, "E369", {"start": v(160.51, 32.16) * mm, "end": v(169.82, 26.78) * mm, "construction": true});
            skLineSegment(sketch, "E370.trimOffspring", {"start": v(157.82, 6) * mm, "end": v(148.51, 11.37) * mm, "construction": true});
            skLineSegment(sketch, "E371.trimOffspring", {"start": v(184.45, -9.38) * mm, "end": v(175.14, -4) * mm, "construction": true});
            skLineSegment(sketch, "E372.trimOffspring", {"start": v(213.77, 1.4) * mm, "end": v(223.08, -3.97) * mm, "construction": true});
            skLineSegment(sketch, "E373.trimOffspring", {"start": v(187.14, 16.78) * mm, "end": v(196.45, 11.4) * mm, "construction": true});
            skCircle(sketch, "E374", {"center": v(153.17, 8.68) * mm, "radius": 2 * mm});
            skCircle(sketch, "E375", {"center": v(165.17, 29.47) * mm, "radius": 2 * mm});
            skCircle(sketch, "E376", {"center": v(191.8, 14.1) * mm, "radius": 2 * mm});
            skCircle(sketch, "E377", {"center": v(179.8, -6.7) * mm, "radius": 2 * mm});
            skCircle(sketch, "E378", {"center": v(206.43, -22.07) * mm, "radius": 2 * mm});
            skCircle(sketch, "E379", {"center": v(218.43, -1.28) * mm, "radius": 2 * mm});
            skArc(sketch, "E380", {"start": v(-431.84, -33.47) * mm, "mid": v(-437.7, -19.32) * mm, "end": v(-451.84, -13.47) * mm});
            skArc(sketch, "E381", {"start": v(-451.84, -13.47) * mm, "mid": v(-461.8, -4.6) * mm, "end": v(-471.83, -13.37) * mm});
            skPoint(sketch, "E382", {"position": v(-471.84, -43.47) * mm});
            skLineSegment(sketch, "E383", {"start": v(-471.84, -53.47) * mm, "end": v(-431.84, -53.47) * mm});
            skPoint(sketch, "E384.orphan", {"position": v(-431.84, -43.47) * mm});
            skCircle(sketch, "E385", {"center": v(-461.84, -43.47) * mm, "radius": 2 * mm});
            skCircle(sketch, "E386", {"center": v(-445.87, -43.47) * mm, "radius": 2 * mm});
            skCircle(sketch, "E387", {"center": v(-461.84, -13.46) * mm, "radius": 2 * mm});
            skCircle(sketch, "E388", {"center": v(-461.84, -23.47) * mm, "radius": 2 * mm});
            skCircle(sketch, "E389", {"center": v(-443.84, -25.56) * mm, "radius": 1.5 * mm});
            skLineSegment(sketch, "E390", {"start": v(-325, 302.96) * mm, "end": v(-297, 302.96) * mm});
            skLineSegment(sketch, "E391", {"start": v(-311, 302.96) * mm, "end": v(-311, 289.9) * mm, "construction": true});
            skLineSegment(sketch, "E392.MirrorCS", {"start": v(-309.17, 291.44) * mm, "end": v(-309.17, 294.44) * mm});
            skLineSegment(sketch, "E393.MirrorCS", {"start": v(-300.95, 291.44) * mm, "end": v(-300.95, 287.57) * mm});
            skLineSegment(sketch, "E394.MirrorCS", {"start": v(-303.94, 291.45) * mm, "end": v(-300.95, 291.44) * mm});
            skLineSegment(sketch, "E395.MirrorCS", {"start": v(-303.94, 289.45) * mm, "end": v(-303.94, 291.45) * mm});
            skLineSegment(sketch, "E396.MirrorCS", {"start": v(-307.14, 291.44) * mm, "end": v(-307.14, 289.44) * mm});
            skLineSegment(sketch, "E397.MirrorCS", {"start": v(-300.95, 294.44) * mm, "end": v(-300.95, 298.32) * mm});
            skLineSegment(sketch, "E398.MirrorCS", {"start": v(-303.94, 296.45) * mm, "end": v(-303.94, 294.44) * mm});
            skLineSegment(sketch, "E399.MirrorCS", {"start": v(-303.94, 294.44) * mm, "end": v(-300.95, 294.44) * mm});
            skLineSegment(sketch, "E400.MirrorCS", {"start": v(-307.14, 294.44) * mm, "end": v(-307.14, 296.44) * mm});
            skLineSegment(sketch, "E401", {"start": v(-325, 282.96) * mm, "end": v(-297, 282.96) * mm});
            skLineSegment(sketch, "E402", {"start": v(-325, 302.96) * mm, "end": v(-325, 282.96) * mm});
            skLineSegment(sketch, "E403.right", {"start": v(-297, 302.96) * mm, "end": v(-297, 282.96) * mm});
            skLineSegment(sketch, "E404", {"start": v(-300.95, 287.57) * mm, "end": v(-297, 287.57) * mm});
            skLineSegment(sketch, "E405", {"start": v(-300.95, 298.32) * mm, "end": v(-297, 298.32) * mm});
            skLineSegment(sketch, "E406.left", {"start": v(-307.14, 296.44) * mm, "end": v(-307.14, 296.45) * mm});
            skLineSegment(sketch, "E406.right", {"start": v(-303.94, 289.44) * mm, "end": v(-303.94, 289.45) * mm});
            skLineSegment(sketch, "E407", {"start": v(-321.05, 287.57) * mm, "end": v(-325, 287.57) * mm});
            skLineSegment(sketch, "E408", {"start": v(-307.14, 289.44) * mm, "end": v(-303.94, 289.45) * mm});
            skLineSegment(sketch, "E409", {"start": v(-309.17, 291.44) * mm, "end": v(-307.14, 291.44) * mm});
            skLineSegment(sketch, "E410", {"start": v(-309.17, 294.44) * mm, "end": v(-307.14, 294.44) * mm});
            skLineSegment(sketch, "E411", {"start": v(-307.14, 296.45) * mm, "end": v(-303.94, 296.45) * mm});
            skLineSegment(sketch, "E412.right", {"start": v(-307.14, 291.44) * mm, "end": v(-307.14, 294.44) * mm});
            skLineSegment(sketch, "E413.bottom", {"start": v(-307.14, 289.44) * mm, "end": v(-303.94, 289.44) * mm});
            skLineSegment(sketch, "E413.left", {"start": v(-307.14, 289.44) * mm, "end": v(-307.14, 296.45) * mm});
            skLineSegment(sketch, "E413.right", {"start": v(-303.94, 289.44) * mm, "end": v(-303.94, 296.45) * mm});
            skLineSegment(sketch, "E414.bottom", {"start": v(-303.94, 291.45) * mm, "end": v(-300.95, 291.45) * mm});
            skLineSegment(sketch, "E414.left", {"start": v(-303.94, 291.45) * mm, "end": v(-303.94, 294.44) * mm});
            skLineSegment(sketch, "E414.right", {"start": v(-300.95, 291.45) * mm, "end": v(-300.95, 294.44) * mm});
            skCircle(sketch, "E415", {"center": v(336.36, 147) * mm, "radius": 1.75 * mm});
            skCircle(sketch, "E416", {"center": v(336.36, 197) * mm, "radius": 1.75 * mm});
            skLineSegment(sketch, "E417", {"start": v(300.35, 144.9) * mm, "end": v(300.65, 185.62) * mm});
            skLineSegment(sketch, "E418.MirrorCS", {"start": v(202.45, 185.62) * mm, "end": v(300.65, 185.62) * mm});
            skLineSegment(sketch, "E419.MirrorCS", {"start": v(300.35, 144.9) * mm, "end": v(202.15, 144.9) * mm});
            skLineSegment(sketch, "E420", {"start": v(202.45, 185.62) * mm, "end": v(202.15, 144.9) * mm});
            skCircle(sketch, "E421", {"center": v(191.17, 147) * mm, "radius": 1.75 * mm});
            skCircle(sketch, "E422", {"center": v(191.36, 196.94) * mm, "radius": 1.75 * mm});
            skCircle(sketch, "E423.MirrorC", {"center": v(326.05, 168.86) * mm, "radius": 10 * mm});
            skLineSegment(sketch, "E424", {"start": v(336.36, 147) * mm, "end": v(191.17, 147) * mm, "construction": true});
            skLineSegment(sketch, "E425", {"start": v(263.76, 147) * mm, "end": v(263.76, 168.23) * mm, "construction": true});
            skLineSegment(sketch, "E426.bottom", {"start": v(175.63, 212.62) * mm, "end": v(352.12, 212.62) * mm});
            skLineSegment(sketch, "E426.left", {"start": v(175.63, 212.62) * mm, "end": v(175.63, 128.15) * mm});
            skLineSegment(sketch, "E427", {"start": v(175.63, 128.15) * mm, "end": v(131.72, 88.6) * mm});
            skLineSegment(sketch, "E428.MirrorCS", {"start": v(352.12, 128.15) * mm, "end": v(396.03, 88.6) * mm});
            skLineSegment(sketch, "E429", {"start": v(352.12, 128.15) * mm, "end": v(352.12, 212.62) * mm});
            skLineSegment(sketch, "E430.trimOffspring", {"start": v(396.03, 88.6) * mm, "end": v(461, 88.6) * mm});
            skCircle(sketch, "E431", {"center": v(-11.84, 227.96) * mm, "radius": 2 * mm});
            skLineSegment(sketch, "E432", {"start": v(33.49, 217.95) * mm, "end": v(19.49, 193.7) * mm});
            skPoint(sketch, "E433.orphan", {"position": v(31.49, 214.49) * mm});
            skLineSegment(sketch, "E434", {"start": v(2.16, 272.22) * mm, "end": v(-25.84, 272.22) * mm});
            skPoint(sketch, "E435.orphan", {"position": v(-1.84, 272.22) * mm});
            skLineSegment(sketch, "E436", {"start": v(-43.17, 193.7) * mm, "end": v(-57.17, 217.95) * mm});
            skPoint(sketch, "E437.orphan", {"position": v(-45.17, 197.17) * mm});
            skLineSegment(sketch, "E438", {"start": v(16.49, 195.43) * mm, "end": v(30.49, 219.68) * mm});
            skLineSegment(sketch, "E439", {"start": v(-25.84, 268.75) * mm, "end": v(2.16, 268.75) * mm});
            skLineSegment(sketch, "E440", {"start": v(-40.17, 195.43) * mm, "end": v(-54.17, 219.68) * mm});
            skSolve(sketch);
        }
        {
            var Q0;
            Q0=makeQuery(id+"F0.imprint","IMPRINT",FACE,{"disambiguationData":[TD([[makeQuery(id+"F0.imprint","IMPRINT",EDGE,{"derivedFrom":sQuery(id+"F0.wireOp",EDGE,"E2")}),1.0]])]});
            var Q1;
            Q1=makeQuery(id+"F0.imprint","IMPRINT",FACE,{"disambiguationData":[TD([[makeQuery(id+"F0.imprint","IMPRINT",EDGE,{"derivedFrom":sQuery(id+"F0.wireOp",EDGE,"E13")}),1.0]])]});
            var Q2;
            Q2=makeQuery(id+"F0.imprint","IMPRINT",FACE,{"disambiguationData":[TD([[makeQuery(id+"F0.imprint","IMPRINT",EDGE,{"derivedFrom":sQuery(id+"F0.wireOp",EDGE,"E0")}),1.0]])]});
            var Q3;
            Q3=makeQuery(id+"F0.imprint","IMPRINT",FACE,{"disambiguationData":[TD([[makeQuery(id+"F0.imprint","IMPRINT",EDGE,{"derivedFrom":sQuery(id+"F0.wireOp",EDGE,"E44")}),1.0]])]});
            var Q4;
            Q4=makeQuery(id+"F0.imprint","IMPRINT",FACE,{"disambiguationData":[TD([[makeQuery(id+"F0.imprint","IMPRINT",EDGE,{"derivedFrom":sQuery(id+"F0.wireOp",EDGE,"E17")}),-1.0]])]});
            var Q5;
            Q5=makeQuery(id+"F0.imprint","IMPRINT",FACE,{"disambiguationData":[TD([[makeQuery(id+"F0.imprint","IMPRINT",EDGE,{"derivedFrom":sQuery(id+"F0.wireOp",EDGE,"E191")}),-1.0]])]});
            var Q6;
            Q6=makeQuery(id+"F0.imprint","IMPRINT",FACE,{"disambiguationData":[TD([[makeQuery(id+"F0.imprint","IMPRINT",EDGE,{"derivedFrom":sQuery(id+"F0.wireOp",EDGE,"E188")}),-1.0]])]});
            var Q7;
            {var subQ0=sQuery(id+"F0.wireOp",EDGE,"E28");Q7=makeQuery(id+"F0.imprint","IMPRINT",FACE,{"disambiguationData":[TD([[makeQuery(id+"F0.imprint","IMPRINT",EDGE,{"derivedFrom":subQ0}),1.0]])]});}
            var Q8;
            {var subQ0=sQuery(id+"F0.wireOp",EDGE,"E23");Q8=makeQuery(id+"F0.imprint","IMPRINT",FACE,{"disambiguationData":[TD([[makeQuery(id+"F0.imprint","IMPRINT",EDGE,{"derivedFrom":subQ0}),1.0]])]});}
            var Q9;
            {var subQ0=sQuery(id+"F0.wireOp",EDGE,"E19");Q9=makeQuery(id+"F0.imprint","IMPRINT",FACE,{"disambiguationData":[TD([[makeQuery(id+"F0.imprint","IMPRINT",EDGE,{"derivedFrom":subQ0}),1.0]])]});}
            var Q10;
            {var subQ24=sQuery(id+"F0.wireOp",EDGE,"E19");Q10=makeQuery(id+"F0.imprint","IMPRINT",FACE,{"disambiguationData":[TD([[makeQuery(id+"F0.imprint","IMPRINT",EDGE,{"derivedFrom":subQ24}),-1.0]])]});}
            var Q11;
            {var subQ0=sQuery(id+"F0.wireOp",EDGE,"E41");Q11=makeQuery(id+"F0.imprint","IMPRINT",FACE,{"disambiguationData":[TD([[makeQuery(id+"F0.imprint","IMPRINT",EDGE,{"derivedFrom":subQ0}),1.0]])]});}
            var Q12;
            {var subQ6=sQuery(id+"F0.wireOp",EDGE,"E34");Q12=makeQuery(id+"F0.imprint","IMPRINT",FACE,{"disambiguationData":[TD([[makeQuery(id+"F0.imprint","IMPRINT",EDGE,{"derivedFrom":subQ6}),-1.0]])]});}
            var Q13;
            {var subQ0=sQuery(id+"F0.wireOp",EDGE,"E37");Q13=makeQuery(id+"F0.imprint","IMPRINT",FACE,{"disambiguationData":[TD([[makeQuery(id+"F0.imprint","IMPRINT",EDGE,{"derivedFrom":subQ0}),1.0]])]});}
            var Q14;
            {var subQ0=sQuery(id+"F0.wireOp",EDGE,"E32");Q14=makeQuery(id+"F0.imprint","IMPRINT",FACE,{"disambiguationData":[TD([[makeQuery(id+"F0.imprint","IMPRINT",EDGE,{"derivedFrom":subQ0}),1.0]])]});}
            var Q15;
            {var subQ4=sQuery(id+"F0.wireOp",EDGE,"E25");Q15=makeQuery(id+"F0.imprint","IMPRINT",FACE,{"disambiguationData":[TD([[makeQuery(id+"F0.imprint","IMPRINT",EDGE,{"derivedFrom":subQ4}),-1.0]])]});}
            var Q16;
            {var subQ26=sQuery(id+"F0.wireOp",EDGE,"E19");Q16=makeQuery(id+"F0.imprint","IMPRINT",FACE,{"disambiguationData":[TD([[makeQuery(id+"F0.imprint","IMPRINT",EDGE,{"derivedFrom":subQ26}),-1.0]])]});}
            var Q17;
            {var subQ0=sQuery(id+"F0.wireOp",EDGE,"E432");var subQ1=sQuery(id+"F0.wireOp",EDGE,"E24");var subQ2=makeQuery(id+"F0.imprint","INTERSECT",VERTEX,{"derivedFrom":[subQ1,subQ0]});Q17=makeQuery(id+"F0.imprint","IMPRINT",FACE,{"disambiguationData":[TD([[makeQuery(id+"F0.imprint","IMPRINT",EDGE,{"disambiguationData":[TD([[subQ2,1.0]])],"derivedFrom":subQ1}),-1.0]])]});}
            var Q18;
            {var subQ0=sQuery(id+"F0.wireOp",EDGE,"E23");Q18=makeQuery(id+"F0.imprint","IMPRINT",FACE,{"disambiguationData":[TD([[makeQuery(id+"F0.imprint","IMPRINT",EDGE,{"derivedFrom":subQ0}),1.0]])]});}
            var Q19;
            {var subQ0=sQuery(id+"F0.wireOp",EDGE,"E434");var subQ1=sQuery(id+"F0.wireOp",EDGE,"E18");var subQ2=makeQuery(id+"F0.imprint","INTERSECT",VERTEX,{"derivedFrom":[subQ1,subQ0]});Q19=makeQuery(id+"F0.imprint","IMPRINT",FACE,{"disambiguationData":[TD([[makeQuery(id+"F0.imprint","IMPRINT",EDGE,{"disambiguationData":[TD([[subQ2,-1.0]])],"derivedFrom":subQ1}),-1.0]])]});}
            var Q20;
            {var subQ0=sQuery(id+"F0.wireOp",EDGE,"E436");var subQ1=sQuery(id+"F0.wireOp",EDGE,"E33");var subQ2=makeQuery(id+"F0.imprint","INTERSECT",VERTEX,{"derivedFrom":[subQ1,subQ0]});Q20=makeQuery(id+"F0.imprint","IMPRINT",FACE,{"disambiguationData":[TD([[makeQuery(id+"F0.imprint","IMPRINT",EDGE,{"disambiguationData":[TD([[subQ2,1.0]])],"derivedFrom":subQ1}),-1.0]])]});}
            extrude(context, id + "F1", {"entities" : qUnion([Q0, Q1, Q2, Q3, Q4, Q5, Q6, Q7, Q8, Q9, Q10, Q11, Q12, Q13, Q14, Q15, Q16, Q17, Q18, Q19, Q20]), "depth" : 4 * mm});
        }
        {
            var Q0;
            Q0=qCreatedBy(makeId("Top.planeOp"),FACE);
            var sketch = newSketch(context, id + "F2", { "sketchPlane" : qUnion([Q0])});
            skCircle(sketch, "E441", {"center": v(-121.85, -375.87) * mm, "radius": 2 * mm});
            skCircle(sketch, "E442", {"center": v(-88.9, -375.87) * mm, "radius": 2 * mm});
            skCircle(sketch, "E443", {"center": v(-172.94, -424.4) * mm, "radius": 2 * mm});
            skCircle(sketch, "E444", {"center": v(-156.46, -395.85) * mm, "radius": 2 * mm});
            skCircle(sketch, "E445", {"center": v(-156.46, -355.9) * mm, "radius": 2 * mm});
            skCircle(sketch, "E446", {"center": v(-172.94, -327.35) * mm, "radius": 2 * mm});
            skCircle(sketch, "E447", {"center": v(-144.92, -375.87) * mm, "radius": 2 * mm});
            skLineSegment(sketch, "E448", {"start": v(-185.74, -319.52) * mm, "end": v(-173.32, -312.35) * mm});
            skArc(sketch, "E449", {"start": v(-162.26, -315.04) * mm, "mid": v(-128.44, -347.33) * mm, "end": v(-83.57, -360.47) * mm});
            skLineSegment(sketch, "E450", {"start": v(-173.32, -439.4) * mm, "end": v(-185.74, -432.23) * mm});
            skArc(sketch, "E451", {"start": v(-83.57, -391.28) * mm, "mid": v(-128.44, -404.42) * mm, "end": v(-162.26, -436.71) * mm});
            skLineSegment(sketch, "E452", {"start": v(-75.7, -368.7) * mm, "end": v(-75.7, -383.04) * mm});
            skArc(sketch, "E453", {"start": v(-188.94, -421.3) * mm, "mid": v(-177.88, -375.87) * mm, "end": v(-188.94, -330.44) * mm});
            skArc(sketch, "E454", {"start": v(-75.7, -368.7) * mm, "mid": v(-77.99, -363.01) * mm, "end": v(-83.57, -360.47) * mm});
            skArc(sketch, "E455", {"start": v(-83.57, -391.28) * mm, "mid": v(-77.99, -388.74) * mm, "end": v(-75.7, -383.04) * mm});
            skArc(sketch, "E456", {"start": v(-173.32, -439.4) * mm, "mid": v(-167.25, -440.27) * mm, "end": v(-162.26, -436.71) * mm});
            skArc(sketch, "E457", {"start": v(-188.94, -421.3) * mm, "mid": v(-189.53, -427.41) * mm, "end": v(-185.74, -432.23) * mm});
            skArc(sketch, "E458", {"start": v(-185.74, -319.52) * mm, "mid": v(-189.53, -324.34) * mm, "end": v(-188.94, -330.44) * mm});
            skArc(sketch, "E459", {"start": v(-162.26, -315.04) * mm, "mid": v(-167.25, -311.48) * mm, "end": v(-173.32, -312.35) * mm});
            skCircle(sketch, "E460", {"center": v(-132, -364.33) * mm, "radius": 1.5 * mm});
            skCircle(sketch, "E461", {"center": v(-132, -387.4) * mm, "radius": 1.5 * mm});
            skCircle(sketch, "E462", {"center": v(-101, -364.33) * mm, "radius": 1.5 * mm});
            skCircle(sketch, "E463", {"center": v(-101, -387.4) * mm, "radius": 1.5 * mm});
            skCircle(sketch, "E464", {"center": v(-141.48, -392.7) * mm, "radius": 1.5 * mm});
            skCircle(sketch, "E465", {"center": v(-161.45, -381.16) * mm, "radius": 1.5 * mm});
            skCircle(sketch, "E466", {"center": v(-156.98, -419.54) * mm, "radius": 1.5 * mm});
            skCircle(sketch, "E467", {"center": v(-176.95, -408) * mm, "radius": 1.5 * mm});
            skCircle(sketch, "E468", {"center": v(-161.33, -370.57) * mm, "radius": 1.5 * mm});
            skCircle(sketch, "E469", {"center": v(-141.36, -359.04) * mm, "radius": 1.5 * mm});
            skCircle(sketch, "E470", {"center": v(-176.83, -343.72) * mm, "radius": 1.5 * mm});
            skCircle(sketch, "E471", {"center": v(-156.86, -332.2) * mm, "radius": 1.5 * mm});
            skSolve(sketch);
        }
        {
            var Q0;
            Q0=makeQuery(id+"F2.imprint","IMPRINT",FACE,{"disambiguationData":[TD([[makeQuery(id+"F2.imprint","IMPRINT",EDGE,{"derivedFrom":sQuery(id+"F2.wireOp",EDGE,"E441")}),1.0]])]});
            extrude(context, id + "F3", {"entities" : qUnion([Q0]), "depth" : 4 * mm});
        }
        {
            var Q0;
            Q0=qCreatedBy(makeId("Top.planeOp"),FACE);
            var sketch = newSketch(context, id + "F4", { "sketchPlane" : qUnion([Q0])});
            skCircle(sketch, "E472", {"center": v(-7.91, 32.96) * mm, "radius": 5.9 * mm});
            skCircle(sketch, "E473", {"center": v(-37.91, -19) * mm, "radius": 5.9 * mm});
            skCircle(sketch, "E474", {"center": v(7.91, 32.96) * mm, "radius": 5.9 * mm});
            skCircle(sketch, "E475", {"center": v(37.91, -19) * mm, "radius": 5.9 * mm});
            skCircle(sketch, "E476", {"center": v(30, -32.7) * mm, "radius": 5.9 * mm});
            skCircle(sketch, "E477", {"center": v(-30, -32.7) * mm, "radius": 5.9 * mm});
            skLineSegment(sketch, "E478", {"start": v(-48.2, -22.75) * mm, "end": v(-38.4, -39.75) * mm});
            skLineSegment(sketch, "E479", {"start": v(-31.47, -43.75) * mm, "end": v(31.47, -43.75) * mm});
            skLineSegment(sketch, "E480", {"start": v(38.4, -39.75) * mm, "end": v(48.2, -22.75) * mm});
            skLineSegment(sketch, "E481", {"start": v(48.2, -14.75) * mm, "end": v(16.74, 39.75) * mm});
            skLineSegment(sketch, "E482", {"start": v(9.81, 43.75) * mm, "end": v(-9.81, 43.75) * mm});
            skLineSegment(sketch, "E483", {"start": v(-16.74, 39.75) * mm, "end": v(-48.2, -14.75) * mm});
            skArc(sketch, "E484", {"start": v(-48.2, -14.75) * mm, "mid": v(-49.28, -18.75) * mm, "end": v(-48.2, -22.75) * mm});
            skArc(sketch, "E485", {"start": v(-9.81, 43.75) * mm, "mid": v(-13.81, 42.68) * mm, "end": v(-16.74, 39.75) * mm});
            skArc(sketch, "E486", {"start": v(16.74, 39.75) * mm, "mid": v(13.81, 42.68) * mm, "end": v(9.81, 43.75) * mm});
            skArc(sketch, "E487", {"start": v(48.2, -22.75) * mm, "mid": v(49.28, -18.75) * mm, "end": v(48.2, -14.75) * mm});
            skArc(sketch, "E488", {"start": v(31.47, -43.75) * mm, "mid": v(35.47, -42.68) * mm, "end": v(38.4, -39.75) * mm});
            skArc(sketch, "E489", {"start": v(-38.4, -39.75) * mm, "mid": v(-35.47, -42.68) * mm, "end": v(-31.47, -43.75) * mm});
            skCircle(sketch, "E490", {"center": v(0, -6.25) * mm, "radius": 15 * mm});
            skCircle(sketch, "E491", {"center": v(0, -34.25) * mm, "radius": 6 * mm});
            skCircle(sketch, "E492", {"center": v(0, 16.25) * mm, "radius": 1.5 * mm});
            skCircle(sketch, "E493", {"center": v(-19.49, -17.5) * mm, "radius": 1.5 * mm});
            skCircle(sketch, "E494", {"center": v(19.49, -17.5) * mm, "radius": 1.5 * mm});
            skSolve(sketch);
        }
        {
            var Q0;
            Q0=makeQuery(id+"F4.imprint","IMPRINT",FACE,{"disambiguationData":[TD([[makeQuery(id+"F4.imprint","IMPRINT",EDGE,{"derivedFrom":sQuery(id+"F4.wireOp",EDGE,"E472")}),1.0]])]});
            extrude(context, id + "F5", {"entities" : qUnion([Q0]), "depth" : 4 * mm});
        }
    });
